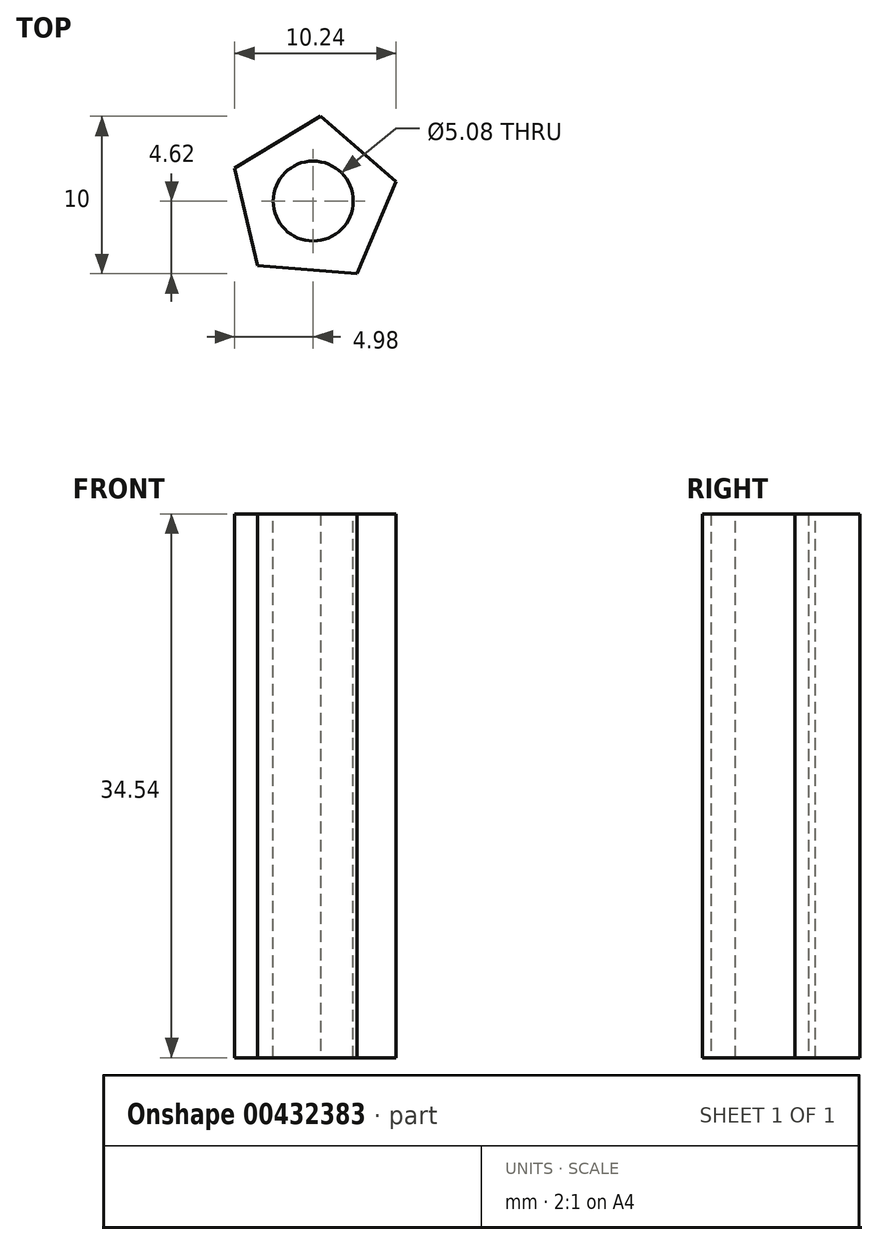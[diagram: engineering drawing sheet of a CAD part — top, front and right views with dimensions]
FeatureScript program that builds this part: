
annotation { "Feature Type Name" : "Feature", "Feature Type Description" : "" }
export const myFeature = defineFeature(function(context is Context, id is Id, definition is map)
    precondition{}
    {
        {
            var Q0;
            Q0=qCreatedBy(makeId("Top.planeOp"),FACE);
            var sketch = newSketch(context, id + "F0", { "sketchPlane" : qUnion([Q0])});
            skCircle(sketch, "E0.cCircle", {"center": v(0, 0) * mm, "radius": 4.37 * mm, "construction": true});
            skLineSegment(sketch, "E0.0", {"start": v(0.45, 5.38) * mm, "end": v(5.26, 1.23) * mm});
            skLineSegment(sketch, "E0.1", {"start": v(5.26, 1.23) * mm, "end": v(2.8, -4.62) * mm});
            skLineSegment(sketch, "E0.2", {"start": v(2.8, -4.62) * mm, "end": v(-3.53, -4.09) * mm});
            skLineSegment(sketch, "E0.3", {"start": v(-3.53, -4.09) * mm, "end": v(-4.98, 2.1) * mm});
            skLineSegment(sketch, "E0.4", {"start": v(-4.98, 2.1) * mm, "end": v(0.45, 5.38) * mm});
            skPoint(sketch, "E0.0.midPoint", {"position": v(2.86, 3.3) * mm});
            skSolve(sketch);
        }
        {
            var Q0;
            Q0=makeQuery(id+"F0.imprint","IMPRINT",FACE,{"disambiguationData":[TD([[makeQuery(id+"F0.imprint","IMPRINT",EDGE,{"derivedFrom":sQuery(id+"F0.wireOp",EDGE,"E0.0")}),-1.0]])]});
            extrude(context, id + "F1", {"entities" : qUnion([Q0]), "depth" : 34.54 * mm});
        }
        {
            var Q0;
            Q0=makeQuery(id+"F1.opExtrude","CAP_FACE",FACE,{"disambiguationData":[OSD([sQuery(id+"F0.wireOp",EDGE,"E0.0"),sQuery(id+"F0.wireOp",EDGE,"E0.1"),sQuery(id+"F0.wireOp",EDGE,"E0.2"),sQuery(id+"F0.wireOp",EDGE,"E0.3"),sQuery(id+"F0.wireOp",EDGE,"E0.4")])],"isStart":false});
            var sketch = newSketch(context, id + "F2", { "sketchPlane" : qUnion([Q0])});
            skCircle(sketch, "E1", {"center": v(0, 0) * mm, "radius": 2.54 * mm});
            skSolve(sketch);
        }
        {
            var Q0;
            Q0 = qSketchRegion(id + "F2", true);
            extrude(context, id + "F3", {"entities" : qUnion([Q0]), "operationType" : NewBodyOperationType.REMOVE, "endBound" : BoundingType.THROUGH_ALL, "oppositeDirection" : true, "depth" : 25.4 * mm});
        }
    });
